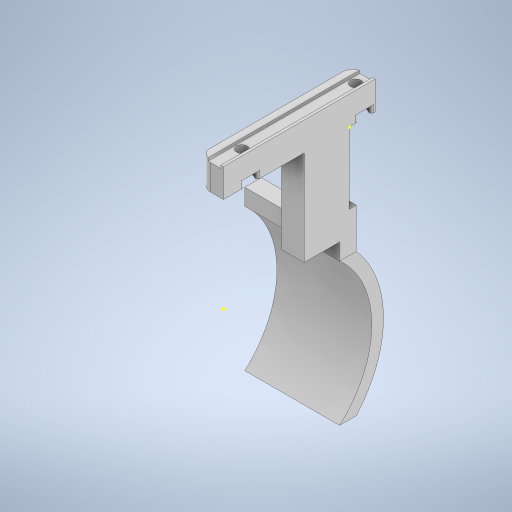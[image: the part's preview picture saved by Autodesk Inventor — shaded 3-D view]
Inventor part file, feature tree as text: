
AUTODESK INVENTOR PART (.ipt)
format: ipt  version: 2024 (Build 280153000, 153)  size: 375,296 bytes
history: native  units: in
note: dims shown in document units (in); Inventor stores cm internally (conversion verified against a paired STEP export)
features: sketch x12, extrude x8, projected_geometry x4, fillet x2, sweep x1
ambient origin geometry x8: Origin, YZ Plane, XZ Plane, XY Plane, X Axis, Y Axis, Z Axis, Center Point
bodies: Solid1 (feature_tree), Solid2 (feature_tree)
feature tree (27):
  extrude  "Extrusion1"  Depth=2.5197in
  extrude  "Extrusion2"  Depth=1.8898in
  extrude  "Extrusion3"  Depth=0.4724in TaperAngle=0.0deg
  fillet  "Fillet1"  Radius=0.0433in
  fillet  "Fillet2"  Radius=0.2126in
  extrude  "Extrusion19"  Depth=0.4724in TaperAngle=0.0deg
  extrude  "Extrusion21"  Depth=0.1181in TaperAngle=0.0deg
  sketch  "Sketch41"  dims[d17=0.1772in d18=0.0394in]
  extrude  "Extrusion22"  Depth=0.0394in
  extrude  "Extrusion25"  Depth=0.4724in
  sweep  "Sweep4"
  extrude  "Extrusion26"  Depth=0.1181in
  sketch  "Sketch60"  dims[d134=1.2008in d135=180.0deg d136=0.2756in d137=1.5748in d138=0.2756in d139=0.2756in d140=0.0in d154=4.1063in d155=0.0in d164=2.3622in d165=1.5748in d166=0.0in d167=0.0in d168=2.4813in d169=0.0in d42=0.0197in d43=0.0344in d44=0.0197in d45=0.0344in d46=0.0in d47=0.0in d48=0.0in d49=0.0in d50=0.0in d51=0.0in d52=0.0in d53=0.0in d55=0.0197in d56=0.0344in d57=0.0197in d58=0.0344in d60=0.0197in d61=0.0344in d62=0.0197in d63=0.0344in d72=0.0197in d73=0.0344in d74=0.0197in d75=0.0344in]
  sketch  "Sketch1"  dims[d1=0.374in d2=2.5197in]
  sketch  "Sketch2"  dims[d3=0.1772in d4=1.8898in]
  sketch  "Sketch3"  dims[d6=0.1457in d7=0.4724in d8=0.0in d9=0.0433in d10=0.2126in]
  projected_geometry  "Projected Loop2"
  projected_geometry  "Projected Loop3"
  projected_geometry  "Projected Loop4"
  projected_geometry  "Projected Loop5"
  sketch  "Sketch28"  dims[d11=0.0472in d12=0.4724in d13=0.0in]
  sketch  "Sketch40"  dims[d14=0.2953in d15=0.1181in d16=0.0in]
  sketch  "Sketch42"  dims[d19=0.1575in d76=0.4724in]
  sketch  "Sketch54"  dims[d107=0.102in d108=0.748in]
  sketch  "Sketch56"  dims[d109=1.1811in d110=0.0in d130=0.1181in]
  sketch  "Sketch58"  dims[d131=0.8661in]
  sketch  "Sketch59"  dims[d132=0.3937in d133=0.0in]
